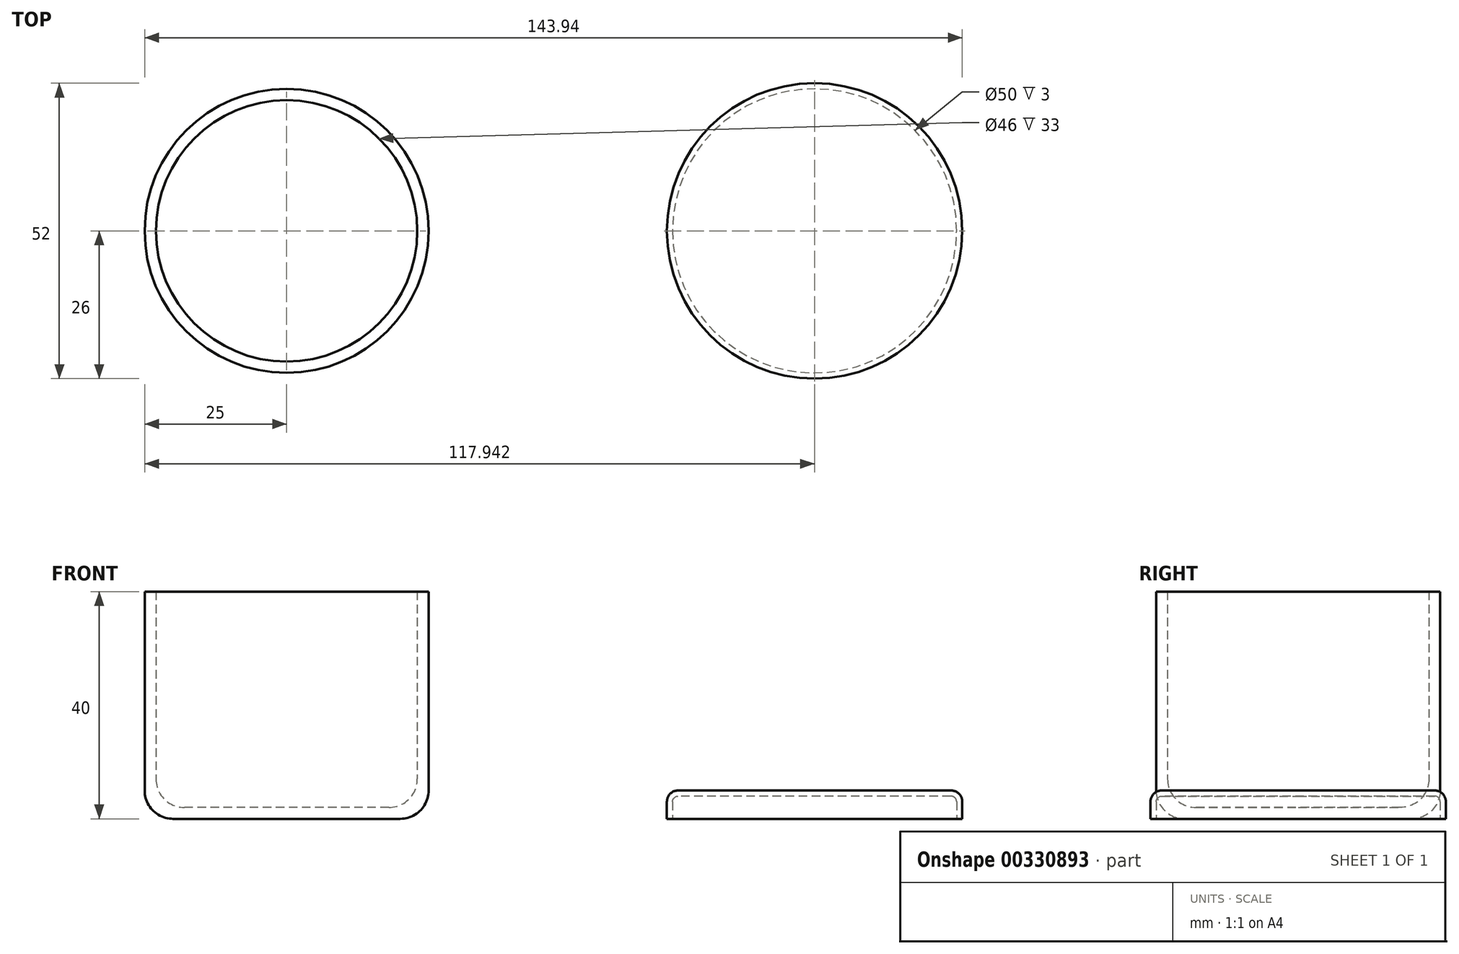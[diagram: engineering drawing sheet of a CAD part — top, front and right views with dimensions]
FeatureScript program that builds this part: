
annotation { "Feature Type Name" : "Feature", "Feature Type Description" : "" }
export const myFeature = defineFeature(function(context is Context, id is Id, definition is map)
    precondition{}
    {
        {
            var Q0;
            Q0=qCreatedBy(makeId("Top.planeOp"),FACE);
            var sketch = newSketch(context, id + "F0", { "sketchPlane" : qUnion([Q0])});
            skCircle(sketch, "E0", {"center": v(0, 0) * mm, "radius": 25 * mm});
            skCircle(sketch, "E1", {"center": v(92.94, 0) * mm, "radius": 26 * mm});
            skSolve(sketch);
        }
        {
            var Q0;
            Q0=makeQuery(id+"F0.imprint","IMPRINT",FACE,{"disambiguationData":[TD([[makeQuery(id+"F0.imprint","IMPRINT",EDGE,{"derivedFrom":sQuery(id+"F0.wireOp",EDGE,"E0")}),1.0]])]});
            extrude(context, id + "F1", {"entities" : qUnion([Q0]), "depth" : 40 * mm});
        }
        {
            var Q0;
            Q0=makeQuery(id+"F0.imprint","IMPRINT",FACE,{"disambiguationData":[TD([[makeQuery(id+"F0.imprint","IMPRINT",EDGE,{"derivedFrom":sQuery(id+"F0.wireOp",EDGE,"E1")}),1.0]])]});
            extrude(context, id + "F2", {"entities" : qUnion([Q0]), "depth" : 5 * mm});
        }
        {
            var Q0;
            Q0=makeQuery(id+"F2.opExtrude","CAP_FACE",FACE,{"disambiguationData":[OSD([sQuery(id+"F0.wireOp",EDGE,"E1")])],"isStart":false});
            fillet(context, id + "F3", {"entities" : qUnion([Q0]), "radius" : 2 * mm, "tangentPropagation" : true, "allowEdgeOverflow" : false});
        }
        {
            var Q0;
            Q0=makeQuery(id+"F1.opExtrude","CAP_FACE",FACE,{"disambiguationData":[OSD([sQuery(id+"F0.wireOp",EDGE,"E0")])],"isStart":false});
            shell(context, id + "F4", {"entities" : qUnion([Q0]), "thickness" : 2 * mm});
        }
        {
            var Q0;
            {var subQ0=sQuery(id+"F0.wireOp",EDGE,"E0");Q0=makeQuery(id+"F4.opShell","OFFSET_EDGE",EDGE,{"disambiguationData":[OSD([subQ0]),TDD([makeQuery(id+"F1.opExtrude","CAP_EDGE",EDGE,{"disambiguationData":[OSD([subQ0])],"isStart":true})])]});}
            fillet(context, id + "F5", {"entities" : qUnion([Q0]), "radius" : 5 * mm, "tangentPropagation" : true, "allowEdgeOverflow" : false});
        }
        {
            var Q0;
            Q0=makeQuery(id+"F1.opExtrude","CAP_EDGE",EDGE,{"disambiguationData":[OSD([sQuery(id+"F0.wireOp",EDGE,"E0")])],"isStart":true});
            fillet(context, id + "F6", {"entities" : qUnion([Q0]), "radius" : 5 * mm, "tangentPropagation" : true, "allowEdgeOverflow" : false});
        }
        {
            var Q0;
            Q0=makeQuery(id+"F2.opExtrude","CAP_FACE",FACE,{"disambiguationData":[OSD([sQuery(id+"F0.wireOp",EDGE,"E1")])],"isStart":true});
            shell(context, id + "F7", {"entities" : qUnion([Q0]), "thickness" : 1 * mm});
        }
    });
